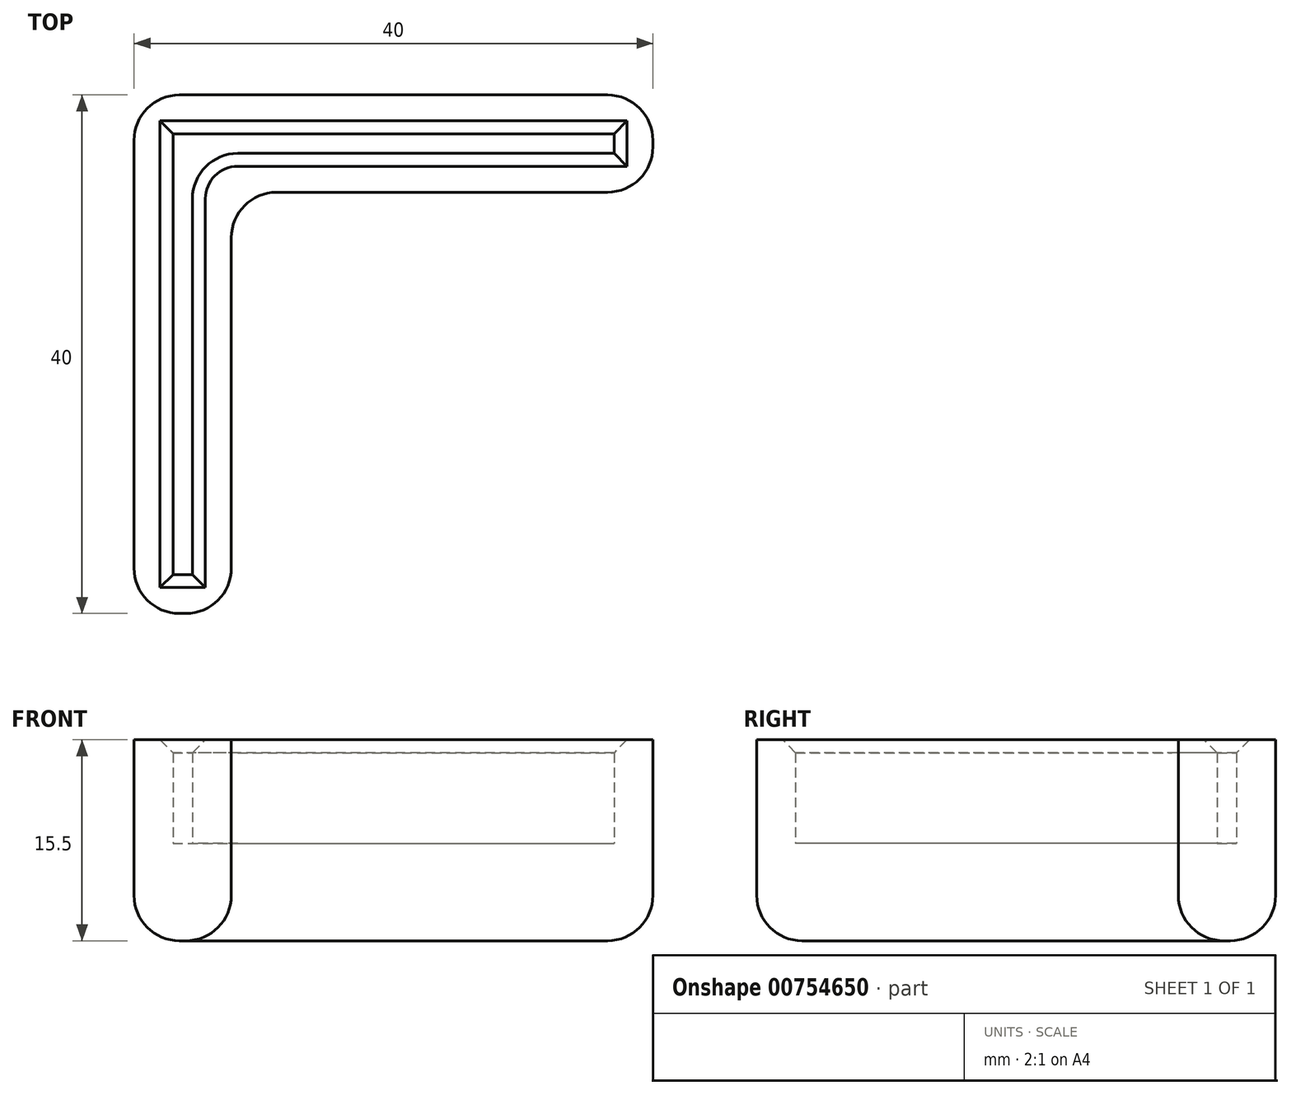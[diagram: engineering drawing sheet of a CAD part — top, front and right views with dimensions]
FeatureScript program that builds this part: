
annotation { "Feature Type Name" : "Feature", "Feature Type Description" : "" }
export const myFeature = defineFeature(function(context is Context, id is Id, definition is map)
    precondition{}
    {
        {
            var Q0;
            Q0=qCreatedBy(makeId("Top.planeOp"),FACE);
            var sketch = newSketch(context, id + "F0", { "sketchPlane" : qUnion([Q0])});
            skLineSegment(sketch, "E0.bottom", {"start": v(1.5, -1.5) * mm, "end": v(34, -1.5) * mm});
            skLineSegment(sketch, "E0.top", {"start": v(0, 0) * mm, "end": v(34, 0) * mm});
            skLineSegment(sketch, "E0.left", {"start": v(0, -1.5) * mm, "end": v(0, 0) * mm});
            skLineSegment(sketch, "E0.right", {"start": v(34, -1.5) * mm, "end": v(34, 0) * mm});
            skLineSegment(sketch, "E1.bottom", {"start": v(0, 0) * mm, "end": v(1.5, 0) * mm});
            skLineSegment(sketch, "E1.top", {"start": v(0, -34) * mm, "end": v(1.5, -34) * mm});
            skLineSegment(sketch, "E1.left", {"start": v(0, 0) * mm, "end": v(0, -34) * mm});
            skLineSegment(sketch, "E1.right", {"start": v(1.5, -1.5) * mm, "end": v(1.5, -34) * mm});
            skLineSegment(sketch, "E2.0", {"start": v(4.5, -4.5) * mm, "end": v(37, -4.5) * mm});
            skLineSegment(sketch, "E2.1", {"start": v(-3, 3) * mm, "end": v(37, 3) * mm});
            skLineSegment(sketch, "E2.2", {"start": v(-3, 3) * mm, "end": v(-3, -37) * mm});
            skLineSegment(sketch, "E2.3", {"start": v(37, -4.5) * mm, "end": v(37, 3) * mm});
            skLineSegment(sketch, "E2.4", {"start": v(-3, -37) * mm, "end": v(4.5, -37) * mm});
            skLineSegment(sketch, "E2.5", {"start": v(4.5, -4.5) * mm, "end": v(4.5, -37) * mm});
            skSolve(sketch);
        }
        {
            var Q0;
            Q0 = qSketchRegion(id + "F0", true);
            extrude(context, id + "F1", {"entities" : qUnion([Q0]), "depth" : 8 * mm, "offsetDistance" : 25 * mm});
        }
        {
            var Q0;
            Q0=makeQuery(id+"F0.imprint","IMPRINT",FACE,{"disambiguationData":[TD([[makeQuery(id+"F0.imprint","IMPRINT",EDGE,{"derivedFrom":sQuery(id+"F0.wireOp",EDGE,"E0.bottom")}),1.0]])]});
            var Q1;
            Q1=makeQuery(id+"F0.imprint","IMPRINT",FACE,{"disambiguationData":[TD([[makeQuery(id+"F0.imprint","IMPRINT",EDGE,{"derivedFrom":sQuery(id+"F0.wireOp",EDGE,"E0.bottom")}),-1.0]])]});
            extrude(context, id + "F2", {"entities" : qUnion([Q0, Q1]), "operationType" : NewBodyOperationType.ADD, "oppositeDirection" : true, "depth" : 7.5 * mm, "offsetDistance" : 25 * mm});
        }
        {
            var Q0;
            Q0=makeQuery(id+"F2.opExtrude","CAP_EDGE",EDGE,{"disambiguationData":[OSD([sQuery(id+"F0.wireOp",EDGE,"E2.0")])],"isStart":false});
            var Q1;
            Q1=makeQuery(id+"F2.opExtrude","CAP_EDGE",EDGE,{"disambiguationData":[OSD([sQuery(id+"F0.wireOp",EDGE,"E2.5")])],"isStart":false});
            var Q2;
            Q2=makeQuery(id+"F2.opExtrude","CAP_EDGE",EDGE,{"disambiguationData":[OSD([sQuery(id+"F0.wireOp",EDGE,"E2.1")])],"isStart":false});
            var Q3;
            Q3=makeQuery(id+"F2.opExtrude","CAP_EDGE",EDGE,{"disambiguationData":[OSD([sQuery(id+"F0.wireOp",EDGE,"E2.2")])],"isStart":false});
            var Q4;
            {var subQ0=sQuery(id+"F0.wireOp",EDGE,"E2.5");var subQ1=sQuery(id+"F0.wireOp",EDGE,"E2.0");Q4=makeQuery(id+"F2.boolean.opBoolean","MERGE",EDGE,{"derivedFrom":[makeQuery(id+"F1.opExtrude","SWEPT_EDGE",EDGE,{"disambiguationData":[OSD([subQ1,subQ0])]}),makeQuery(id+"F2.opExtrude","SWEPT_EDGE",EDGE,{"disambiguationData":[OSD([subQ1,subQ0])]})]});}
            var Q5;
            {var subQ0=sQuery(id+"F0.wireOp",EDGE,"E2.2");var subQ1=sQuery(id+"F0.wireOp",EDGE,"E2.1");Q5=makeQuery(id+"F2.boolean.opBoolean","MERGE",EDGE,{"derivedFrom":[makeQuery(id+"F1.opExtrude","SWEPT_EDGE",EDGE,{"disambiguationData":[OSD([subQ1,subQ0])]}),makeQuery(id+"F2.opExtrude","SWEPT_EDGE",EDGE,{"disambiguationData":[OSD([subQ1,subQ0])]})]});}
            var Q6;
            Q6=makeQuery(id+"F2.opExtrude","CAP_EDGE",EDGE,{"disambiguationData":[OSD([sQuery(id+"F0.wireOp",EDGE,"E2.4")])],"isStart":false});
            var Q7;
            Q7=makeQuery(id+"F2.opExtrude","CAP_EDGE",EDGE,{"disambiguationData":[OSD([sQuery(id+"F0.wireOp",EDGE,"E2.3")])],"isStart":false});
            var Q8;
            {var subQ0=sQuery(id+"F0.wireOp",EDGE,"E2.5");var subQ1=sQuery(id+"F0.wireOp",EDGE,"E2.4");Q8=makeQuery(id+"F2.boolean.opBoolean","MERGE",EDGE,{"derivedFrom":[makeQuery(id+"F1.opExtrude","SWEPT_EDGE",EDGE,{"disambiguationData":[OSD([subQ1,subQ0])]}),makeQuery(id+"F2.opExtrude","SWEPT_EDGE",EDGE,{"disambiguationData":[OSD([subQ1,subQ0])]})]});}
            var Q9;
            {var subQ0=sQuery(id+"F0.wireOp",EDGE,"E2.4");var subQ1=sQuery(id+"F0.wireOp",EDGE,"E2.2");Q9=makeQuery(id+"F2.boolean.opBoolean","MERGE",EDGE,{"derivedFrom":[makeQuery(id+"F1.opExtrude","SWEPT_EDGE",EDGE,{"disambiguationData":[OSD([subQ1,subQ0])]}),makeQuery(id+"F2.opExtrude","SWEPT_EDGE",EDGE,{"disambiguationData":[OSD([subQ1,subQ0])]})]});}
            var Q10;
            {var subQ0=sQuery(id+"F0.wireOp",EDGE,"E2.3");var subQ1=sQuery(id+"F0.wireOp",EDGE,"E2.0");Q10=makeQuery(id+"F2.boolean.opBoolean","MERGE",EDGE,{"derivedFrom":[makeQuery(id+"F1.opExtrude","SWEPT_EDGE",EDGE,{"disambiguationData":[OSD([subQ1,subQ0])]}),makeQuery(id+"F2.opExtrude","SWEPT_EDGE",EDGE,{"disambiguationData":[OSD([subQ1,subQ0])]})]});}
            var Q11;
            {var subQ0=sQuery(id+"F0.wireOp",EDGE,"E2.3");var subQ1=sQuery(id+"F0.wireOp",EDGE,"E2.1");Q11=makeQuery(id+"F2.boolean.opBoolean","MERGE",EDGE,{"derivedFrom":[makeQuery(id+"F1.opExtrude","SWEPT_EDGE",EDGE,{"disambiguationData":[OSD([subQ1,subQ0])]}),makeQuery(id+"F2.opExtrude","SWEPT_EDGE",EDGE,{"disambiguationData":[OSD([subQ1,subQ0])]})]});}
            var Q12;
            Q12=makeQuery(id+"F1.opExtrude","SWEPT_EDGE",EDGE,{"disambiguationData":[OSD([sQuery(id+"F0.wireOp",EDGE,"E0.bottom"),sQuery(id+"F0.wireOp",EDGE,"E1.right")])]});
            fillet(context, id + "F3", {"entities" : qUnion([Q0, Q1, Q2, Q3, Q4, Q5, Q6, Q7, Q8, Q9, Q10, Q11, Q12]), "radius" : 3.5 * mm, "tangentPropagation" : true, "allowEdgeOverflow" : false});
        }
        {
            var Q0;
            Q0=makeQuery(id+"F1.opExtrude","CAP_EDGE",EDGE,{"disambiguationData":[OSD([sQuery(id+"F0.wireOp",EDGE,"E1.left")])],"isStart":false});
            var Q1;
            {var subQ0=sQuery(id+"F0.wireOp",EDGE,"E1.right");var subQ1=sQuery(id+"F0.wireOp",EDGE,"E0.bottom");Q1=makeQuery(id+"F3.opFillet","BLEND_EDGE",EDGE,{"blendedFrom":[makeQuery(id+"F1.opExtrude","SWEPT_EDGE",EDGE,{"disambiguationData":[OSD([subQ1,subQ0])]}),makeQuery(id+"F1.opExtrude","CAP_FACE",FACE,{"disambiguationData":[OSD([subQ1,sQuery(id+"F0.wireOp",EDGE,"E0.top"),sQuery(id+"F0.wireOp",EDGE,"E0.right"),sQuery(id+"F0.wireOp",EDGE,"E1.bottom"),sQuery(id+"F0.wireOp",EDGE,"E1.top"),sQuery(id+"F0.wireOp",EDGE,"E1.left"),subQ0,sQuery(id+"F0.wireOp",EDGE,"E2.0"),sQuery(id+"F0.wireOp",EDGE,"E2.1"),sQuery(id+"F0.wireOp",EDGE,"E2.2"),sQuery(id+"F0.wireOp",EDGE,"E2.3"),sQuery(id+"F0.wireOp",EDGE,"E2.4"),sQuery(id+"F0.wireOp",EDGE,"E2.5")])],"isStart":false})],"blendedInto":[makeQuery(id+"F1.opExtrude","CAP_FACE",FACE,{"disambiguationData":[OSD([subQ1,sQuery(id+"F0.wireOp",EDGE,"E0.top"),sQuery(id+"F0.wireOp",EDGE,"E0.right"),sQuery(id+"F0.wireOp",EDGE,"E1.bottom"),sQuery(id+"F0.wireOp",EDGE,"E1.top"),sQuery(id+"F0.wireOp",EDGE,"E1.left"),subQ0,sQuery(id+"F0.wireOp",EDGE,"E2.0"),sQuery(id+"F0.wireOp",EDGE,"E2.1"),sQuery(id+"F0.wireOp",EDGE,"E2.2"),sQuery(id+"F0.wireOp",EDGE,"E2.3"),sQuery(id+"F0.wireOp",EDGE,"E2.4"),sQuery(id+"F0.wireOp",EDGE,"E2.5")])],"isStart":false})]});}
            var Q2;
            Q2=makeQuery(id+"F1.opExtrude","CAP_EDGE",EDGE,{"disambiguationData":[OSD([sQuery(id+"F0.wireOp",EDGE,"E0.top"),sQuery(id+"F0.wireOp",EDGE,"E1.bottom")])],"isStart":false});
            var Q3;
            Q3=makeQuery(id+"F1.opExtrude","CAP_EDGE",EDGE,{"disambiguationData":[OSD([sQuery(id+"F0.wireOp",EDGE,"E1.top")])],"isStart":false});
            var Q4;
            Q4=makeQuery(id+"F1.opExtrude","CAP_EDGE",EDGE,{"disambiguationData":[OSD([sQuery(id+"F0.wireOp",EDGE,"E0.right")])],"isStart":false});
            chamfer(context, id + "F4", {"entities" : qUnion([Q0, Q1, Q2, Q3, Q4]), "width" : 1 * mm, "tangentPropagation" : true});
        }
    });
